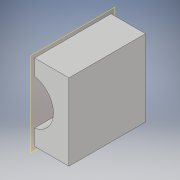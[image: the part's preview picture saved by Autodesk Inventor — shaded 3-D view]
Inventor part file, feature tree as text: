
AUTODESK INVENTOR PART (.ipt)
format: ipt  version: 2019.3 (Build 233278000, 278)  size: 97,280 bytes
history: native  units: mm
features: extrude x1, plane x1, split x1, sketch x1
ambient origin geometry x8: Origin, YZ Plane, XZ Plane, XY Plane, X Axis, Y Axis, Z Axis, Center Point
bodies: Solid1 (feature_tree)
feature tree (4):
  extrude  "Extrusion1"  Depth=20.0mm
  plane  "Work Plane1"
  split  "Split1"
  sketch  "Sketch1"  dims[d0=11.9mm d1=20.0mm d2=20.0mm d3=20.0mm d4=0.0mm d5=1.0mm]
